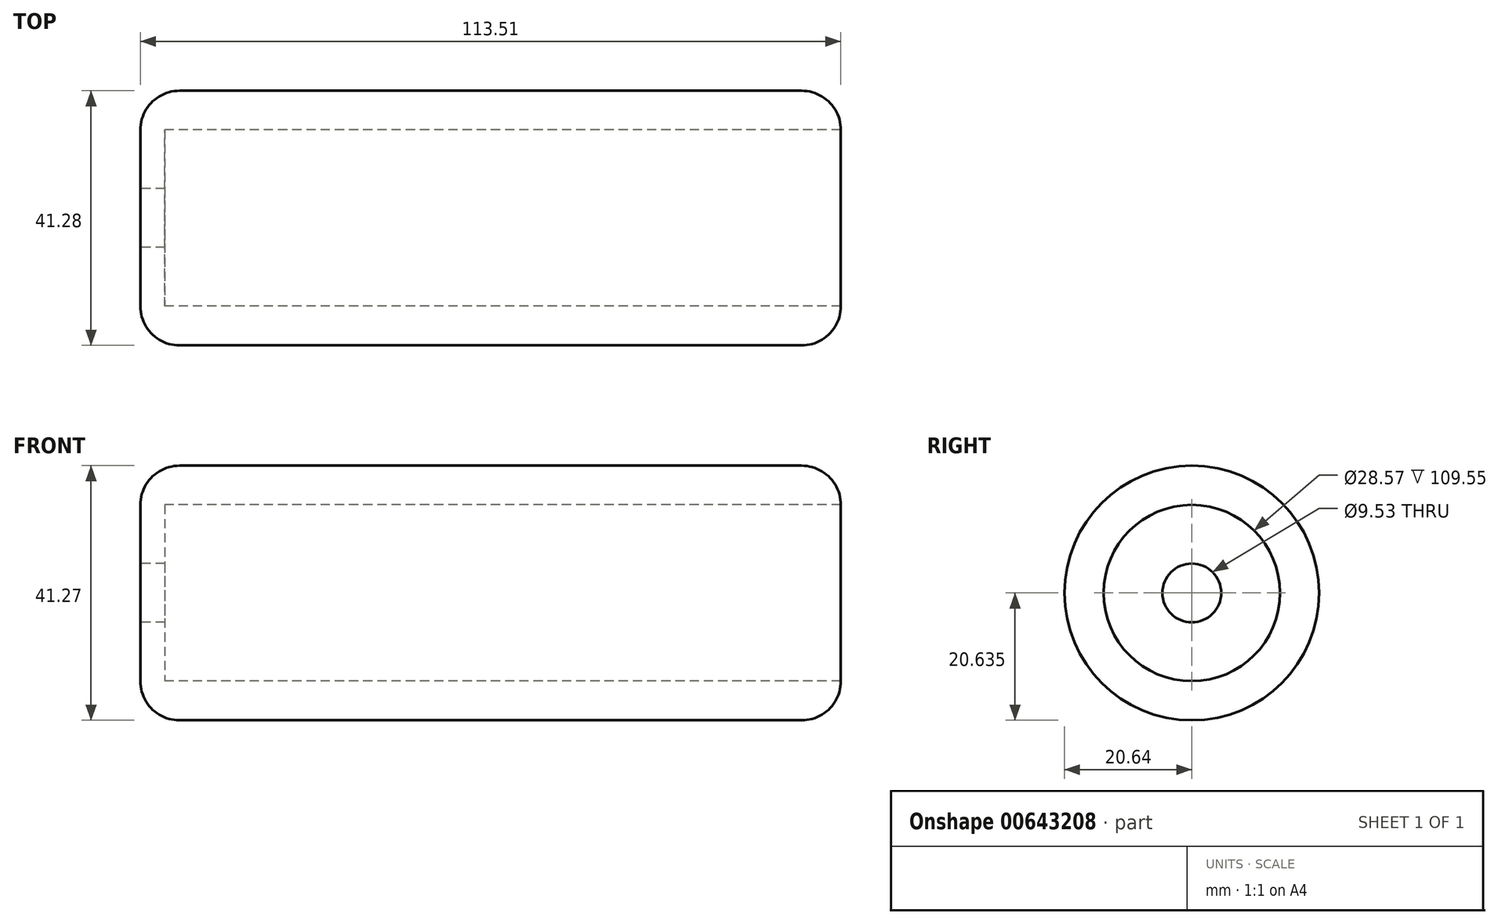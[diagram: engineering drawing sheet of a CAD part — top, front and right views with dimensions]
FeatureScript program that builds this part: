
annotation { "Feature Type Name" : "Feature", "Feature Type Description" : "" }
export const myFeature = defineFeature(function(context is Context, id is Id, definition is map)
    precondition{}
    {
        {
            var Q0;
            Q0=qCreatedBy(makeId("Front.planeOp"),FACE);
            var sketch = newSketch(context, id + "F0", { "sketchPlane" : qUnion([Q0])});
            skLineSegment(sketch, "E0", {"start": v(-48.21, -35.43) * mm, "end": v(65.3, -35.43) * mm});
            skLineSegment(sketch, "E1", {"start": v(65.3, -35.43) * mm, "end": v(65.3, -29.08) * mm});
            skLineSegment(sketch, "E2", {"start": v(65.3, -29.08) * mm, "end": v(-44.25, -29.08) * mm});
            skLineSegment(sketch, "E3", {"start": v(-44.25, -29.08) * mm, "end": v(-44.25, -19.56) * mm});
            skLineSegment(sketch, "E4", {"start": v(-44.25, -19.56) * mm, "end": v(-48.21, -19.56) * mm});
            skLineSegment(sketch, "E5", {"start": v(-48.21, -19.56) * mm, "end": v(-48.21, -35.43) * mm});
            skLineSegment(sketch, "E6", {"start": v(-49.8, -14.8) * mm, "end": v(69.91, -14.8) * mm, "construction": true});
            skSolve(sketch);
        }
        {
            var Q0;
            Q0 = qSketchRegion(id + "F0", true);
            var Q1;
            Q1=sQuery(id+"F0.wireOp",EDGE,"E6");
            revolve(context, id + "F1", {"entities" : qUnion([Q0]), "axis" : qUnion([Q1]), "revolveType" : RevolveType.FULL});
        }
        {
            var Q0;
            Q0=makeQuery(id+"F1.opRevolve","SWEPT_EDGE",EDGE,{"disambiguationData":[OSD([sQuery(id+"F0.wireOp",EDGE,"E0"),sQuery(id+"F0.wireOp",EDGE,"E5")])]});
            var Q1;
            Q1=makeQuery(id+"F1.opRevolve","SWEPT_EDGE",EDGE,{"disambiguationData":[OSD([sQuery(id+"F0.wireOp",EDGE,"E0"),sQuery(id+"F0.wireOp",EDGE,"E1")])]});
            fillet(context, id + "F2", {"entities" : qUnion([Q0, Q1]), "radius" : 6.35 * mm, "tangentPropagation" : true, "allowEdgeOverflow" : false});
        }
    });
